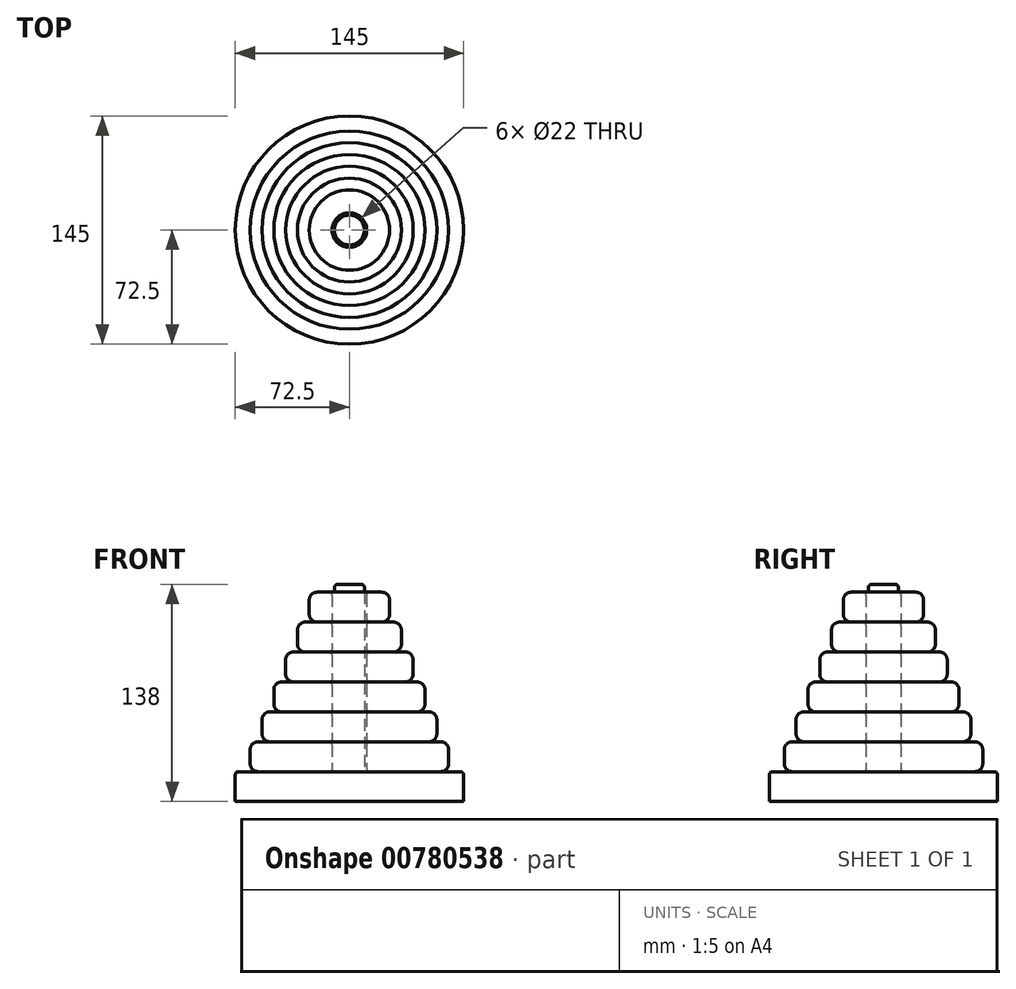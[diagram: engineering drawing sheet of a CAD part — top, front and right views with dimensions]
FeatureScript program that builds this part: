
annotation { "Feature Type Name" : "Feature", "Feature Type Description" : "" }
export const myFeature = defineFeature(function(context is Context, id is Id, definition is map)
    precondition{}
    {
        {
            var Q0;
            Q0=qCreatedBy(makeId("Top.planeOp"),FACE);
            var sketch = newSketch(context, id + "F0", { "sketchPlane" : qUnion([Q0])});
            skCircle(sketch, "E0", {"center": v(0, 0) * mm, "radius": 72.5 * mm});
            skSolve(sketch);
        }
        {
            var Q0;
            Q0 = qSketchRegion(id + "F0", true);
            extrude(context, id + "F1", {"entities" : qUnion([Q0]), "depth" : 19 * mm, "offsetDistance" : 25 * mm});
        }
        {
            var Q0;
            Q0=makeQuery(id+"F1.opExtrude","CAP_FACE",FACE,{"disambiguationData":[OSD([sQuery(id+"F0.wireOp",EDGE,"E0")])],"isStart":false});
            var sketch = newSketch(context, id + "F2", { "sketchPlane" : qUnion([Q0])});
            skCircle(sketch, "E1", {"center": v(0, 0) * mm, "radius": 9.5 * mm});
            skSolve(sketch);
        }
        {
            var Q0;
            Q0 = qSketchRegion(id + "F2", true);
            extrude(context, id + "F3", {"entities" : qUnion([Q0]), "operationType" : NewBodyOperationType.ADD, "depth" : 119 * mm, "offsetDistance" : 25 * mm});
        }
        {
            var Q0;
            Q0=makeQuery(id+"F1.opExtrude","CAP_EDGE",EDGE,{"disambiguationData":[OSD([sQuery(id+"F0.wireOp",EDGE,"E0")])],"isStart":false});
            var Q1;
            Q1=makeQuery(id+"F3.opExtrude","CAP_EDGE",EDGE,{"disambiguationData":[OSD([sQuery(id+"F2.wireOp",EDGE,"E1")])],"isStart":false});
            fillet(context, id + "F4", {"entities" : qUnion([Q0, Q1]), "tangentPropagation" : true, "radius" : 2 * mm, "defaultsChanged" : true, "vertexSettings" : [], "allowEdgeOverflow" : false});
        }
        {
            var Q0;
            Q0=makeQuery(id+"F1.opExtrude","CAP_FACE",FACE,{"disambiguationData":[OSD([sQuery(id+"F0.wireOp",EDGE,"E0")])],"isStart":false});
            var sketch = newSketch(context, id + "F5", { "sketchPlane" : qUnion([Q0])});
            skCircle(sketch, "E2.0", {"center": v(0, 0) * mm, "radius": 11 * mm});
            skCircle(sketch, "E3.0", {"center": v(0, 0) * mm, "radius": 63 * mm});
            skSolve(sketch);
        }
        {
            var Q0;
            Q0 = qSketchRegion(id + "F5", true);
            extrude(context, id + "F6", {"entities" : qUnion([Q0]), "depth" : 19 * mm, "offsetDistance" : 25 * mm});
        }
        {
            var Q0;
            Q0=makeQuery(id+"F6.opExtrude","CAP_FACE",FACE,{"disambiguationData":[OSD([sQuery(id+"F5.wireOp",EDGE,"cc564de0-fd88-43c0-9a8c-3cb1e1811f0d.0"),sQuery(id+"F5.wireOp",EDGE,"E2.0")])],"isStart":false});
            var sketch = newSketch(context, id + "F7", { "sketchPlane" : qUnion([Q0])});
            skCircle(sketch, "E4.0", {"center": v(0, 0) * mm, "radius": 11 * mm});
            skCircle(sketch, "E5.0", {"center": v(0, 0) * mm, "radius": 55.5 * mm});
            skSolve(sketch);
        }
        {
            var Q0;
            Q0 = qSketchRegion(id + "F7", true);
            extrude(context, id + "F8", {"entities" : qUnion([Q0]), "depth" : 19 * mm, "offsetDistance" : 25 * mm});
        }
        {
            var Q0;
            Q0=makeQuery(id+"F8.opExtrude","CAP_FACE",FACE,{"disambiguationData":[OSD([sQuery(id+"F7.wireOp",EDGE,"E4.0"),sQuery(id+"F7.wireOp",EDGE,"E5.0")])],"isStart":false});
            var sketch = newSketch(context, id + "F9", { "sketchPlane" : qUnion([Q0])});
            skCircle(sketch, "E6.0", {"center": v(0, 0) * mm, "radius": 48 * mm});
            skCircle(sketch, "E7.0", {"center": v(0, 0) * mm, "radius": 11 * mm});
            skSolve(sketch);
        }
        {
            var Q0;
            Q0 = qSketchRegion(id + "F9", true);
            extrude(context, id + "F10", {"entities" : qUnion([Q0]), "depth" : 19 * mm, "offsetDistance" : 25 * mm});
        }
        {
            var Q0;
            Q0=makeQuery(id+"F10.opExtrude","CAP_FACE",FACE,{"disambiguationData":[OSD([sQuery(id+"F9.wireOp",EDGE,"E6.0"),sQuery(id+"F9.wireOp",EDGE,"E7.0")])],"isStart":false});
            var sketch = newSketch(context, id + "F11", { "sketchPlane" : qUnion([Q0])});
            skCircle(sketch, "E8.0", {"center": v(0, 0) * mm, "radius": 11 * mm});
            skCircle(sketch, "E9.0", {"center": v(0, 0) * mm, "radius": 40.5 * mm});
            skSolve(sketch);
        }
        {
            var Q0;
            Q0 = qSketchRegion(id + "F11", true);
            extrude(context, id + "F12", {"entities" : qUnion([Q0]), "depth" : 19 * mm, "offsetDistance" : 25 * mm});
        }
        {
            var Q0;
            Q0=makeQuery(id+"F12.opExtrude","CAP_FACE",FACE,{"disambiguationData":[OSD([sQuery(id+"F11.wireOp",EDGE,"E8.0"),sQuery(id+"F11.wireOp",EDGE,"E9.0")])],"isStart":false});
            var sketch = newSketch(context, id + "F13", { "sketchPlane" : qUnion([Q0])});
            skCircle(sketch, "E10.0", {"center": v(0, 0) * mm, "radius": 11 * mm});
            skCircle(sketch, "E11.0", {"center": v(0, 0) * mm, "radius": 33 * mm});
            skSolve(sketch);
        }
        {
            var Q0;
            Q0 = qSketchRegion(id + "F13", true);
            extrude(context, id + "F14", {"entities" : qUnion([Q0]), "depth" : 19 * mm, "offsetDistance" : 25 * mm});
        }
        {
            var Q0;
            Q0=makeQuery(id+"F14.opExtrude","CAP_FACE",FACE,{"disambiguationData":[OSD([sQuery(id+"F13.wireOp",EDGE,"E10.0"),sQuery(id+"F13.wireOp",EDGE,"E11.0")])],"isStart":false});
            var sketch = newSketch(context, id + "F15", { "sketchPlane" : qUnion([Q0])});
            skCircle(sketch, "E12.0", {"center": v(0, 0) * mm, "radius": 11 * mm});
            skCircle(sketch, "E13.0", {"center": v(0, 0) * mm, "radius": 25.5 * mm});
            skSolve(sketch);
        }
        {
            var Q0;
            Q0 = qSketchRegion(id + "F15", true);
            extrude(context, id + "F16", {"entities" : qUnion([Q0]), "depth" : 19 * mm, "offsetDistance" : 25 * mm});
        }
        {
            var Q0;
            Q0=makeQuery(id+"F6.opExtrude","SWEPT_FACE",FACE,{"disambiguationData":[OSD([sQuery(id+"F5.wireOp",EDGE,"E3.0")])]});
            var Q1;
            Q1=makeQuery(id+"F8.opExtrude","SWEPT_FACE",FACE,{"disambiguationData":[OSD([sQuery(id+"F7.wireOp",EDGE,"E5.0")])]});
            var Q2;
            Q2=makeQuery(id+"F10.opExtrude","SWEPT_FACE",FACE,{"disambiguationData":[OSD([sQuery(id+"F9.wireOp",EDGE,"E6.0")])]});
            var Q3;
            Q3=makeQuery(id+"F12.opExtrude","SWEPT_FACE",FACE,{"disambiguationData":[OSD([sQuery(id+"F11.wireOp",EDGE,"E9.0")])]});
            var Q4;
            Q4=makeQuery(id+"F14.opExtrude","SWEPT_FACE",FACE,{"disambiguationData":[OSD([sQuery(id+"F13.wireOp",EDGE,"E11.0")])]});
            var Q5;
            Q5=makeQuery(id+"F16.opExtrude","SWEPT_FACE",FACE,{"disambiguationData":[OSD([sQuery(id+"F15.wireOp",EDGE,"E13.0")])]});
            fillet(context, id + "F17", {"entities" : qUnion([Q0, Q1, Q2, Q3, Q4, Q5]), "tangentPropagation" : true, "radius" : 5 * mm, "defaultsChanged" : false, "vertexSettings" : [], "allowEdgeOverflow" : false});
        }
        {
            var Q0;
            Q0=makeQuery(id+"F6.opExtrude","SWEPT_FACE",FACE,{"disambiguationData":[OSD([sQuery(id+"F5.wireOp",EDGE,"E2.0")])]});
            var Q1;
            Q1=makeQuery(id+"F8.opExtrude","SWEPT_FACE",FACE,{"disambiguationData":[OSD([sQuery(id+"F7.wireOp",EDGE,"E4.0")])]});
            var Q2;
            Q2=makeQuery(id+"F16.opExtrude","SWEPT_FACE",FACE,{"disambiguationData":[OSD([sQuery(id+"F15.wireOp",EDGE,"E12.0")])]});
            var Q3;
            Q3=makeQuery(id+"F14.opExtrude","SWEPT_FACE",FACE,{"disambiguationData":[OSD([sQuery(id+"F13.wireOp",EDGE,"E10.0")])]});
            var Q4;
            Q4=makeQuery(id+"F12.opExtrude","SWEPT_FACE",FACE,{"disambiguationData":[OSD([sQuery(id+"F11.wireOp",EDGE,"E8.0")])]});
            var Q5;
            Q5=makeQuery(id+"F10.opExtrude","SWEPT_FACE",FACE,{"disambiguationData":[OSD([sQuery(id+"F9.wireOp",EDGE,"E7.0")])]});
            fillet(context, id + "F18", {"entities" : qUnion([Q0, Q1, Q2, Q3, Q4, Q5]), "tangentPropagation" : true, "radius" : 2 * mm, "defaultsChanged" : false, "vertexSettings" : [], "allowEdgeOverflow" : false});
        }
    });
